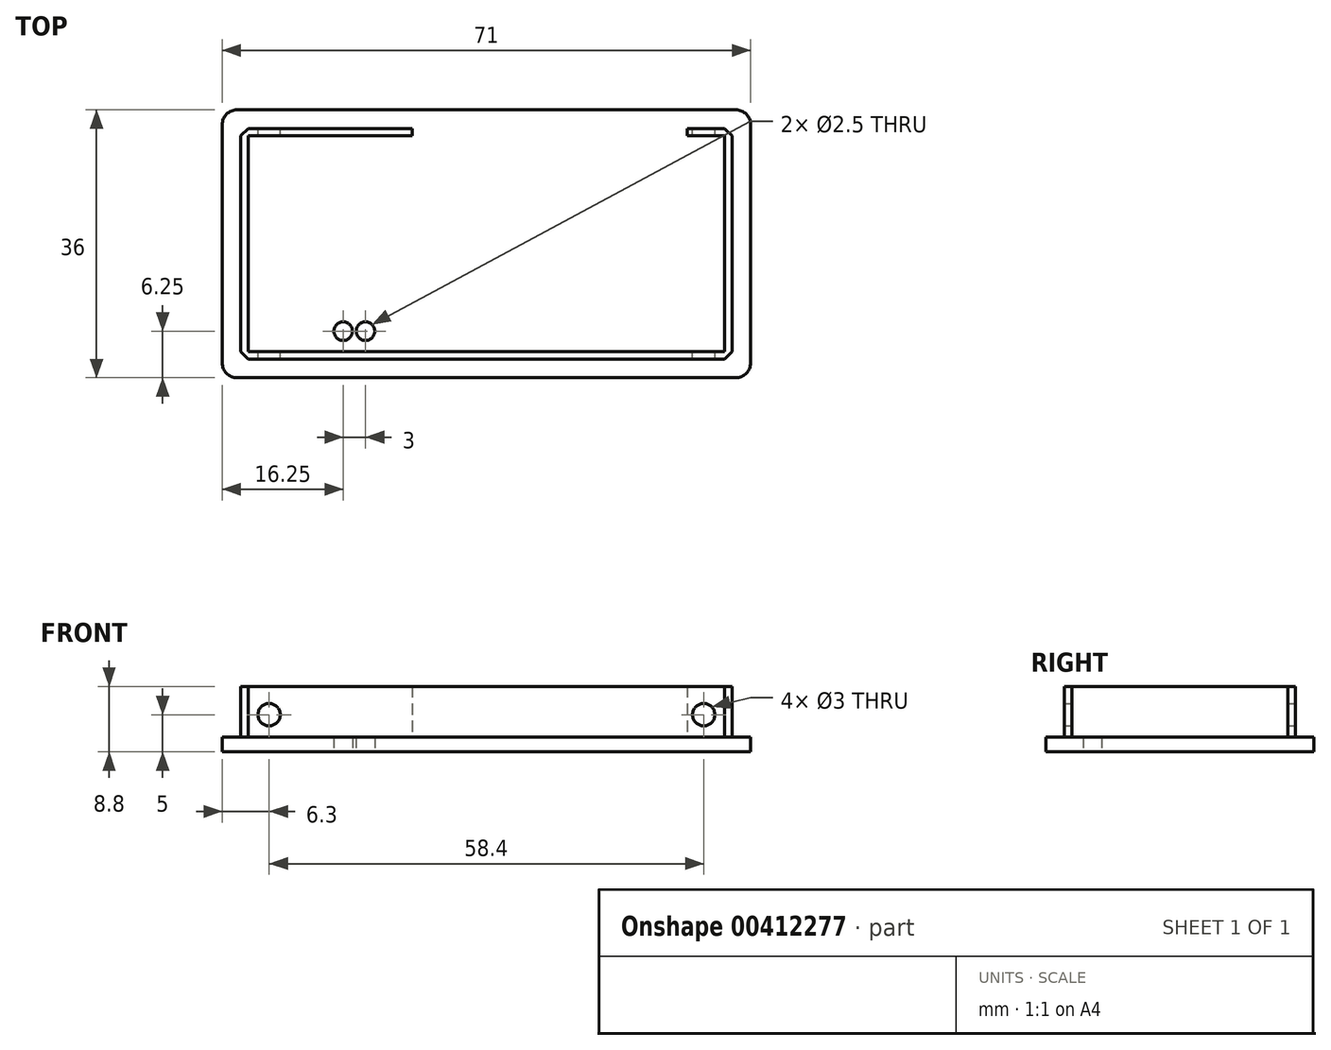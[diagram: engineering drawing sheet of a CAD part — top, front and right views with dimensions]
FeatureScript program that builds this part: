
annotation { "Feature Type Name" : "Feature", "Feature Type Description" : "" }
export const myFeature = defineFeature(function(context is Context, id is Id, definition is map)
    precondition{}
    {
        {
            var Q0;
            Q0=qCreatedBy(makeId("Top.planeOp"),FACE);
            var sketch = newSketch(context, id + "F0", { "sketchPlane" : qUnion([Q0])});
            skLineSegment(sketch, "E0.bottom", {"start": v(0, 0) * mm, "end": v(71, 0) * mm});
            skLineSegment(sketch, "E0.top", {"start": v(0, -36) * mm, "end": v(71, -36) * mm});
            skLineSegment(sketch, "E0.left", {"start": v(0, 0) * mm, "end": v(0, -36) * mm});
            skLineSegment(sketch, "E0.right", {"start": v(71, 0) * mm, "end": v(71, -36) * mm});
            skSolve(sketch);
        }
        {
            var Q0;
            Q0=qSketchRegion(id+"F0",true);
            extrude(context, id + "F1", {"entities" : qUnion([Q0]), "depth" : 2 * mm});
        }
        {
            var Q0;
            Q0=makeQuery(id+"F1.opExtrude","CAP_FACE",FACE,{"disambiguationData":[OSD([sQuery(id+"F0.wireOp",EDGE,"E0.bottom"),sQuery(id+"F0.wireOp",EDGE,"E0.top"),sQuery(id+"F0.wireOp",EDGE,"E0.left"),sQuery(id+"F0.wireOp",EDGE,"E0.right")])],"isStart":false});
            var sketch = newSketch(context, id + "F2", { "sketchPlane" : qUnion([Q0])});
            skLineSegment(sketch, "E1.bottom", {"start": v(2.5, -2.5) * mm, "end": v(25.5, -2.5) * mm});
            skLineSegment(sketch, "E1.top", {"start": v(2.5, -33.5) * mm, "end": v(68.5, -33.5) * mm});
            skLineSegment(sketch, "E1.left", {"start": v(2.5, -2.5) * mm, "end": v(2.5, -33.5) * mm});
            skLineSegment(sketch, "E1.right", {"start": v(68.5, -2.5) * mm, "end": v(68.5, -33.5) * mm});
            skLineSegment(sketch, "E2.bottom", {"start": v(3.5, -3.5) * mm, "end": v(25.5, -3.5) * mm});
            skLineSegment(sketch, "E2.top", {"start": v(3.5, -32.5) * mm, "end": v(67.5, -32.5) * mm});
            skLineSegment(sketch, "E2.left", {"start": v(3.5, -3.5) * mm, "end": v(3.5, -32.5) * mm});
            skLineSegment(sketch, "E2.right", {"start": v(67.5, -3.5) * mm, "end": v(67.5, -32.5) * mm});
            skLineSegment(sketch, "E3.right", {"start": v(62.5, -2.5) * mm, "end": v(62.5, -3.5) * mm});
            skLineSegment(sketch, "E4.trimOffspring", {"start": v(62.5, -2.5) * mm, "end": v(68.5, -2.5) * mm});
            skLineSegment(sketch, "E5.trimOffspring", {"start": v(62.5, -3.5) * mm, "end": v(67.5, -3.5) * mm});
            skLineSegment(sketch, "E6", {"start": v(25.5, -2.5) * mm, "end": v(25.5, -3.5) * mm});
            skPoint(sketch, "E3.left.start.orphan", {"position": v(35.5, -2.5) * mm});
            skSolve(sketch);
        }
        {
            var Q0;
            Q0=qSketchRegion(id+"F2",true);
            extrude(context, id + "F3", {"entities" : qUnion([Q0]), "operationType" : NewBodyOperationType.ADD, "depth" : 6.8 * mm});
        }
        {
            var Q0;
            Q0=makeQuery(id+"F1.opExtrude","SWEPT_EDGE",EDGE,{"disambiguationData":[OSD([sQuery(id+"F0.wireOp",EDGE,"E0.top"),sQuery(id+"F0.wireOp",EDGE,"E0.left")])]});
            var Q1;
            Q1=makeQuery(id+"F1.opExtrude","SWEPT_EDGE",EDGE,{"disambiguationData":[OSD([sQuery(id+"F0.wireOp",EDGE,"E0.bottom"),sQuery(id+"F0.wireOp",EDGE,"E0.left")])]});
            var Q2;
            Q2=makeQuery(id+"F1.opExtrude","SWEPT_EDGE",EDGE,{"disambiguationData":[OSD([sQuery(id+"F0.wireOp",EDGE,"E0.top"),sQuery(id+"F0.wireOp",EDGE,"E0.right")])]});
            var Q3;
            Q3=makeQuery(id+"F1.opExtrude","SWEPT_EDGE",EDGE,{"disambiguationData":[OSD([sQuery(id+"F0.wireOp",EDGE,"E0.bottom"),sQuery(id+"F0.wireOp",EDGE,"E0.right")])]});
            fillet(context, id + "F4", {"entities" : qUnion([Q0, Q1, Q2, Q3]), "radius" : 2 * mm, "tangentPropagation" : true, "allowEdgeOverflow" : false});
        }
        {
            var Q0;
            Q0=makeQuery(id+"F1.opExtrude","CAP_FACE",FACE,{"disambiguationData":[OSD([sQuery(id+"F0.wireOp",EDGE,"E0.bottom"),sQuery(id+"F0.wireOp",EDGE,"E0.top"),sQuery(id+"F0.wireOp",EDGE,"E0.left"),sQuery(id+"F0.wireOp",EDGE,"E0.right")])],"isStart":true});
            var sketch = newSketch(context, id + "F5", { "sketchPlane" : qUnion([Q0])});
            skCircle(sketch, "E7", {"center": v(16.25, 29.75) * mm, "radius": 1.25 * mm});
            skCircle(sketch, "E8", {"center": v(19.25, 29.75) * mm, "radius": 1.25 * mm});
            skSolve(sketch);
        }
        {
            var Q0;
            Q0=qSketchRegion(id+"F5",true);
            extrude(context, id + "F6", {"entities" : qUnion([Q0]), "operationType" : NewBodyOperationType.REMOVE, "endBound" : BoundingType.THROUGH_ALL, "oppositeDirection" : true, "depth" : 25 * mm});
        }
        {
            var Q0;
            Q0=makeQuery(id+"F3.opExtrude","SWEPT_FACE",FACE,{"disambiguationData":[OSD([sQuery(id+"F2.wireOp",EDGE,"E1.bottom")])]});
            var sketch = newSketch(context, id + "F7", { "sketchPlane" : qUnion([Q0])});
            skCircle(sketch, "E9", {"center": v(-64.7, 5) * mm, "radius": 1.5 * mm});
            skCircle(sketch, "E10", {"center": v(-6.3, 5) * mm, "radius": 1.5 * mm});
            skSolve(sketch);
        }
        {
            var Q0;
            Q0=qSketchRegion(id+"F7",true);
            extrude(context, id + "F8", {"entities" : qUnion([Q0]), "operationType" : NewBodyOperationType.REMOVE, "endBound" : BoundingType.THROUGH_ALL, "oppositeDirection" : true, "depth" : 25 * mm});
        }
        {
            var Q0;
            Q0=makeQuery(id+"F3.opExtrude","SWEPT_EDGE",EDGE,{"disambiguationData":[OSD([sQuery(id+"F2.wireOp",EDGE,"E1.bottom"),sQuery(id+"F2.wireOp",EDGE,"E1.left")])]});
            var Q1;
            Q1=makeQuery(id+"F3.opExtrude","SWEPT_EDGE",EDGE,{"disambiguationData":[OSD([sQuery(id+"F2.wireOp",EDGE,"E1.top"),sQuery(id+"F2.wireOp",EDGE,"E1.right")])]});
            var Q2;
            Q2=makeQuery(id+"F3.opExtrude","SWEPT_EDGE",EDGE,{"disambiguationData":[OSD([sQuery(id+"F2.wireOp",EDGE,"E1.right"),sQuery(id+"F2.wireOp",EDGE,"E4.trimOffspring")])]});
            var Q3;
            Q3=makeQuery(id+"F3.opExtrude","SWEPT_EDGE",EDGE,{"disambiguationData":[OSD([sQuery(id+"F2.wireOp",EDGE,"E1.bottom"),sQuery(id+"F2.wireOp",EDGE,"E1.left")])]});
            var Q4;
            Q4=makeQuery(id+"F3.opExtrude","SWEPT_EDGE",EDGE,{"disambiguationData":[OSD([sQuery(id+"F2.wireOp",EDGE,"E1.top"),sQuery(id+"F2.wireOp",EDGE,"E1.left")])]});
            var Q5;
            Q5=makeQuery(id+"F3.opExtrude","SWEPT_EDGE",EDGE,{"disambiguationData":[OSD([sQuery(id+"F2.wireOp",EDGE,"E1.top"),sQuery(id+"F2.wireOp",EDGE,"E1.right")])]});
            chamfer(context, id + "F9", {"entities" : qUnion([Q0, Q1, Q2, Q3, Q4, Q5]), "width" : 1 * mm, "tangentPropagation" : true});
        }
    });
